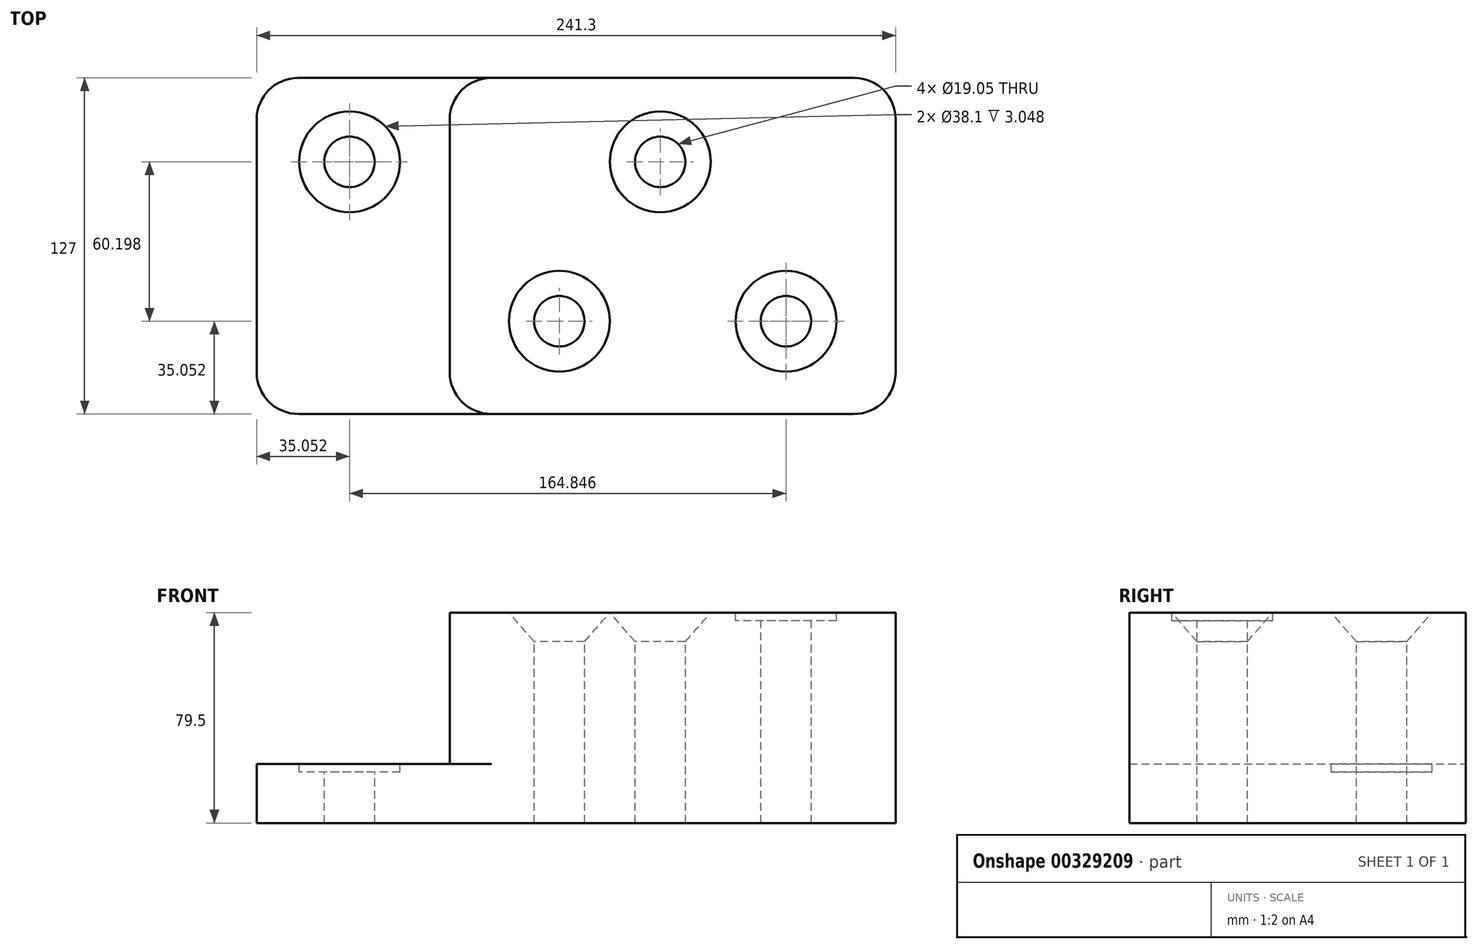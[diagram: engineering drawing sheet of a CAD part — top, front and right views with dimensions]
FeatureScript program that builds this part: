
annotation { "Feature Type Name" : "Feature", "Feature Type Description" : "" }
export const myFeature = defineFeature(function(context is Context, id is Id, definition is map)
    precondition{}
    {
        {
            var Q0;
            Q0=qCreatedBy(makeId("Front.planeOp"),FACE);
            var sketch = newSketch(context, id + "F0", { "sketchPlane" : qUnion([Q0])});
            skLineSegment(sketch, "E0", {"start": v(0, 0) * mm, "end": v(241.3, 0) * mm});
            skLineSegment(sketch, "E1", {"start": v(241.3, 0) * mm, "end": v(241.3, 79.5) * mm});
            skLineSegment(sketch, "E2", {"start": v(241.3, 79.5) * mm, "end": v(72.9, 79.5) * mm});
            skLineSegment(sketch, "E3", {"start": v(72.9, 79.5) * mm, "end": v(72.9, 22.35) * mm});
            skLineSegment(sketch, "E4", {"start": v(72.9, 22.35) * mm, "end": v(0, 22.35) * mm});
            skLineSegment(sketch, "E5", {"start": v(0, 22.35) * mm, "end": v(0, 0) * mm});
            skSolve(sketch);
        }
        {
            var Q0;
            Q0 = qSketchRegion(id + "F0", true);
            extrude(context, id + "F1", {"entities" : qUnion([Q0]), "depth" : 127 * mm});
        }
        {
            var Q0;
            Q0=makeQuery(id+"F1.opExtrude","SWEPT_FACE",FACE,{"disambiguationData":[OSD([sQuery(id+"F0.wireOp",EDGE,"E2")])]});
            var sketch = newSketch(context, id + "F2", { "sketchPlane" : qUnion([Q0])});
            skPoint(sketch, "E6", {"position": v(152.4, -31.75) * mm});
            skPoint(sketch, "E7", {"position": v(114.3, -91.95) * mm});
            skPoint(sketch, "E8", {"position": v(199.9, -91.95) * mm});
            skSolve(sketch);
        }
        {
            var Q0;
            Q0=makeQuery(id+"F1.opExtrude","CAP_EDGE",EDGE,{"disambiguationData":[OSD([sQuery(id+"F0.wireOp",EDGE,"E5")])],"isStart":false});
            var Q1;
            Q1=makeQuery(id+"F1.opExtrude","CAP_EDGE",EDGE,{"disambiguationData":[OSD([sQuery(id+"F0.wireOp",EDGE,"E5")])],"isStart":true});
            var Q2;
            Q2=makeQuery(id+"F1.opExtrude","CAP_EDGE",EDGE,{"disambiguationData":[OSD([sQuery(id+"F0.wireOp",EDGE,"E3")])],"isStart":true});
            var Q3;
            Q3=makeQuery(id+"F1.opExtrude","CAP_EDGE",EDGE,{"disambiguationData":[OSD([sQuery(id+"F0.wireOp",EDGE,"E3")])],"isStart":false});
            var Q4;
            Q4=makeQuery(id+"F1.opExtrude","CAP_EDGE",EDGE,{"disambiguationData":[OSD([sQuery(id+"F0.wireOp",EDGE,"E1")])],"isStart":false});
            var Q5;
            Q5=makeQuery(id+"F1.opExtrude","CAP_EDGE",EDGE,{"disambiguationData":[OSD([sQuery(id+"F0.wireOp",EDGE,"E1")])],"isStart":true});
            fillet(context, id + "F3", {"entities" : qUnion([Q0, Q1, Q2, Q3, Q4, Q5]), "radius" : 15.75 * mm, "tangentPropagation" : true, "allowEdgeOverflow" : false});
        }
        {
            var Q0;
            Q0=sQuery(id+"F2.wireOp",VERTEX,"E6");
            var Q1;
            Q1=sQuery(id+"F2.wireOp",VERTEX,"E7");
            var Q2;
            Q2=makeQuery(id+"F1.opExtrude","SWEPT_BODY",BODY,{"disambiguationData":[OSD([sQuery(id+"F0.wireOp",EDGE,"E0"),sQuery(id+"F0.wireOp",EDGE,"E1"),sQuery(id+"F0.wireOp",EDGE,"E2"),sQuery(id+"F0.wireOp",EDGE,"E3"),sQuery(id+"F0.wireOp",EDGE,"E4"),sQuery(id+"F0.wireOp",EDGE,"E5")])]});
            hole(context, id + "F4", {"style" : HoleStyle.C_SINK, "endStyle" : HoleEndStyle.THROUGH, "holeDiameter" : 19.05 * mm, "cSinkDiameter" : 38.1 * mm, "cSinkAngle" : 82 * degree, "tappedDepth" : 12.7 * mm, "tapClearance" : 3, "locations" : qUnion([Q0, Q1]), "scope" : qUnion([Q2])});
        }
        {
            var Q0;
            Q0=makeQuery(id+"F1.opExtrude","SWEPT_FACE",FACE,{"disambiguationData":[OSD([sQuery(id+"F0.wireOp",EDGE,"E2")])]});
            var sketch = newSketch(context, id + "F5", { "sketchPlane" : qUnion([Q0])});
            skPoint(sketch, "E9", {"position": v(199.9, -91.95) * mm});
            skSolve(sketch);
        }
        {
            var Q0;
            Q0=sQuery(id+"F5.wireOp",VERTEX,"E9");
            var Q1;
            Q1=makeQuery(id+"F1.opExtrude","SWEPT_BODY",BODY,{"disambiguationData":[OSD([sQuery(id+"F0.wireOp",EDGE,"E0"),sQuery(id+"F0.wireOp",EDGE,"E1"),sQuery(id+"F0.wireOp",EDGE,"E2"),sQuery(id+"F0.wireOp",EDGE,"E3"),sQuery(id+"F0.wireOp",EDGE,"E4"),sQuery(id+"F0.wireOp",EDGE,"E5")])]});
            hole(context, id + "F6", {"style" : HoleStyle.C_BORE, "endStyle" : HoleEndStyle.THROUGH, "holeDiameter" : 19.05 * mm, "cBoreDiameter" : 38.1 * mm, "cBoreDepth" : 3.05 * mm, "tappedDepth" : 12.7 * mm, "tapClearance" : 3, "locations" : qUnion([Q0]), "scope" : qUnion([Q1])});
        }
        {
            var Q0;
            Q0=makeQuery(id+"F1.opExtrude","SWEPT_FACE",FACE,{"disambiguationData":[OSD([sQuery(id+"F0.wireOp",EDGE,"E4")])]});
            var sketch = newSketch(context, id + "F7", { "sketchPlane" : qUnion([Q0])});
            skPoint(sketch, "E10", {"position": v(35.05, -31.75) * mm});
            skSolve(sketch);
        }
        {
            var Q0;
            Q0=sQuery(id+"F7.wireOp",VERTEX,"E10");
            var Q1;
            Q1=makeQuery(id+"F1.opExtrude","SWEPT_BODY",BODY,{"disambiguationData":[OSD([sQuery(id+"F0.wireOp",EDGE,"E0"),sQuery(id+"F0.wireOp",EDGE,"E1"),sQuery(id+"F0.wireOp",EDGE,"E2"),sQuery(id+"F0.wireOp",EDGE,"E3"),sQuery(id+"F0.wireOp",EDGE,"E4"),sQuery(id+"F0.wireOp",EDGE,"E5")])]});
            hole(context, id + "F8", {"style" : HoleStyle.C_BORE, "endStyle" : HoleEndStyle.THROUGH, "holeDiameter" : 19.05 * mm, "cBoreDiameter" : 38.1 * mm, "cBoreDepth" : 3.05 * mm, "tappedDepth" : 12.7 * mm, "tapClearance" : 3, "locations" : qUnion([Q0]), "scope" : qUnion([Q1])});
        }
    });
